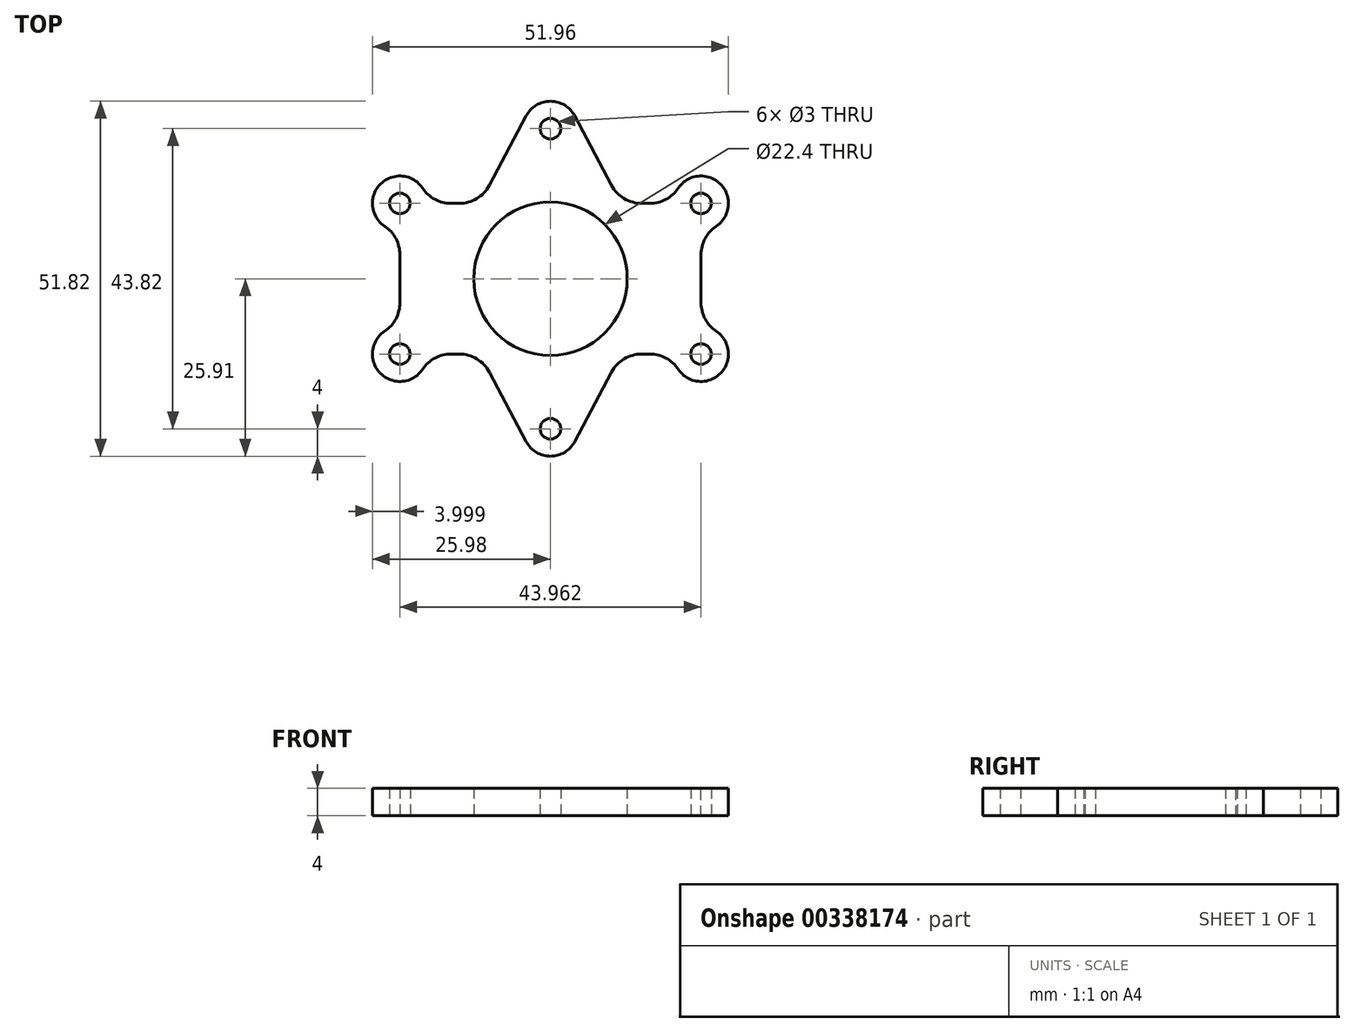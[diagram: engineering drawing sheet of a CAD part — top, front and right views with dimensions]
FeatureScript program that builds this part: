
annotation { "Feature Type Name" : "Feature", "Feature Type Description" : "" }
export const myFeature = defineFeature(function(context is Context, id is Id, definition is map)
    precondition{}
    {
        {
            var Q0;
            Q0=qCreatedBy(makeId("Top.planeOp"),FACE);
            var sketch = newSketch(context, id + "F0", { "sketchPlane" : qUnion([Q0])});
            skLineSegment(sketch, "E0.bottom", {"start": v(21.98, -11) * mm, "end": v(2.1, -11) * mm});
            skLineSegment(sketch, "E0.top", {"start": v(21.98, 11) * mm, "end": v(2.1, 11) * mm});
            skLineSegment(sketch, "E0.left", {"start": v(21.98, -11) * mm, "end": v(21.98, 11) * mm});
            skLineSegment(sketch, "E0.right", {"start": v(-21.98, -11) * mm, "end": v(-21.98, 11) * mm});
            skPoint(sketch, "E0.middle", {"position": v(0, 0) * mm});
            skCircle(sketch, "E1", {"center": v(0, 0) * mm, "radius": 11.2 * mm});
            skCircle(sketch, "E2", {"center": v(-21.98, 11) * mm, "radius": 1.5 * mm});
            skCircle(sketch, "E3", {"center": v(-21.98, -11) * mm, "radius": 1.5 * mm});
            skCircle(sketch, "E4", {"center": v(21.98, -11) * mm, "radius": 1.5 * mm});
            skCircle(sketch, "E5", {"center": v(21.98, 11) * mm, "radius": 1.5 * mm});
            skCircle(sketch, "E6", {"center": v(21.98, 11) * mm, "radius": 4 * mm});
            skCircle(sketch, "E7", {"center": v(21.98, -11) * mm, "radius": 4 * mm});
            skCircle(sketch, "E8", {"center": v(-21.98, -11) * mm, "radius": 4 * mm});
            skCircle(sketch, "E9", {"center": v(-21.98, 11) * mm, "radius": 4 * mm});
            skPoint(sketch, "E10", {"position": v(0, 21.91) * mm});
            skPoint(sketch, "E11", {"position": v(0, -21.91) * mm});
            skCircle(sketch, "E12", {"center": v(0, 21.91) * mm, "radius": 1.5 * mm});
            skCircle(sketch, "E13", {"center": v(0, -21.91) * mm, "radius": 1.5 * mm});
            skCircle(sketch, "E14", {"center": v(0, 21.91) * mm, "radius": 4 * mm});
            skCircle(sketch, "E15", {"center": v(0, -21.91) * mm, "radius": 4 * mm});
            skLineSegment(sketch, "E16", {"start": v(-21.98, 11) * mm, "end": v(-3.53, -23.78) * mm});
            skLineSegment(sketch, "E17", {"start": v(21.98, 11) * mm, "end": v(3.53, -23.78) * mm});
            skLineSegment(sketch, "E18", {"start": v(21.98, -11) * mm, "end": v(3.53, 23.78) * mm});
            skLineSegment(sketch, "E19", {"start": v(-21.98, -11) * mm, "end": v(-3.53, 23.78) * mm});
            skLineSegment(sketch, "E20.trimOffspring", {"start": v(-2.1, 11) * mm, "end": v(-21.98, 11) * mm});
            skLineSegment(sketch, "E21.trimOffspring", {"start": v(-2.1, -11) * mm, "end": v(-21.98, -11) * mm});
            skSolve(sketch);
        }
        {
            var Q0;
            {var subQ0=sQuery(id+"F0.wireOp",EDGE,"E21.trimOffspring");var subQ1=sQuery(id+"F0.wireOp",EDGE,"E8");var subQ2=makeQuery(id+"F0.imprint","INTERSECT",VERTEX,{"derivedFrom":[subQ1,subQ0]});Q0=makeQuery(id+"F0.imprint","IMPRINT",FACE,{"disambiguationData":[TD([[makeQuery(id+"F0.imprint","IMPRINT",EDGE,{"disambiguationData":[TD([[subQ2,-1.0]])],"derivedFrom":subQ1}),-1.0]])]});}
            var Q1;
            {var subQ5=sQuery(id+"F0.wireOp",EDGE,"E0.right");var subQ7=sQuery(id+"F0.wireOp",EDGE,"E8");var subQ8=makeQuery(id+"F0.imprint","INTERSECT",VERTEX,{"derivedFrom":[subQ5,subQ7]});Q1=makeQuery(id+"F0.imprint","IMPRINT",FACE,{"disambiguationData":[TD([[makeQuery(id+"F0.imprint","IMPRINT",EDGE,{"disambiguationData":[TD([[subQ8,-1.0]])],"derivedFrom":subQ5}),-1.0]])]});}
            var Q2;
            {var subQ0=sQuery(id+"F0.wireOp",EDGE,"E20.trimOffspring");var subQ1=sQuery(id+"F0.wireOp",EDGE,"E9");var subQ2=makeQuery(id+"F0.imprint","INTERSECT",VERTEX,{"derivedFrom":[subQ1,subQ0]});Q2=makeQuery(id+"F0.imprint","IMPRINT",FACE,{"disambiguationData":[TD([[makeQuery(id+"F0.imprint","IMPRINT",EDGE,{"disambiguationData":[TD([[subQ2,1.0]])],"derivedFrom":subQ1}),-1.0]])]});}
            var Q3;
            {var subQ0=sQuery(id+"F0.wireOp",EDGE,"E20.trimOffspring");var subQ1=sQuery(id+"F0.wireOp",EDGE,"E2");var subQ2=makeQuery(id+"F0.imprint","INTERSECT",VERTEX,{"derivedFrom":[subQ1,subQ0]});Q3=makeQuery(id+"F0.imprint","IMPRINT",FACE,{"disambiguationData":[TD([[makeQuery(id+"F0.imprint","IMPRINT",EDGE,{"disambiguationData":[TD([[subQ2,1.0]])],"derivedFrom":subQ1}),-1.0]])]});}
            var Q4;
            {var subQ0=sQuery(id+"F0.wireOp",EDGE,"E9");var subQ1=sQuery(id+"F0.wireOp",EDGE,"E0.right");var subQ2=makeQuery(id+"F0.imprint","INTERSECT",VERTEX,{"derivedFrom":[subQ1,subQ0]});Q4=makeQuery(id+"F0.imprint","IMPRINT",FACE,{"disambiguationData":[TD([[makeQuery(id+"F0.imprint","IMPRINT",EDGE,{"disambiguationData":[TD([[subQ2,-1.0]])],"derivedFrom":subQ1}),1.0]])]});}
            var Q5;
            {var subQ0=sQuery(id+"F0.wireOp",EDGE,"E9");var subQ1=sQuery(id+"F0.wireOp",EDGE,"E0.right");var subQ2=makeQuery(id+"F0.imprint","INTERSECT",VERTEX,{"derivedFrom":[subQ1,subQ0]});Q5=makeQuery(id+"F0.imprint","IMPRINT",FACE,{"disambiguationData":[TD([[makeQuery(id+"F0.imprint","IMPRINT",EDGE,{"disambiguationData":[TD([[subQ2,-1.0]])],"derivedFrom":subQ1}),-1.0]])]});}
            var Q6;
            {var subQ0=sQuery(id+"F0.wireOp",EDGE,"E8");var subQ1=sQuery(id+"F0.wireOp",EDGE,"E0.right");var subQ2=makeQuery(id+"F0.imprint","INTERSECT",VERTEX,{"derivedFrom":[subQ1,subQ0]});Q6=makeQuery(id+"F0.imprint","IMPRINT",FACE,{"disambiguationData":[TD([[makeQuery(id+"F0.imprint","IMPRINT",EDGE,{"disambiguationData":[TD([[subQ2,1.0]])],"derivedFrom":subQ1}),-1.0]])]});}
            var Q7;
            {var subQ0=sQuery(id+"F0.wireOp",EDGE,"E19");var subQ1=sQuery(id+"F0.wireOp",EDGE,"E3");var subQ2=makeQuery(id+"F0.imprint","INTERSECT",VERTEX,{"derivedFrom":[subQ1,subQ0]});Q7=makeQuery(id+"F0.imprint","IMPRINT",FACE,{"disambiguationData":[TD([[makeQuery(id+"F0.imprint","IMPRINT",EDGE,{"disambiguationData":[TD([[subQ2,1.0]])],"derivedFrom":subQ1}),-1.0]])]});}
            var Q8;
            {var subQ0=sQuery(id+"F0.wireOp",EDGE,"E8");var subQ1=sQuery(id+"F0.wireOp",EDGE,"E0.right");var subQ2=makeQuery(id+"F0.imprint","INTERSECT",VERTEX,{"derivedFrom":[subQ1,subQ0]});Q8=makeQuery(id+"F0.imprint","IMPRINT",FACE,{"disambiguationData":[TD([[makeQuery(id+"F0.imprint","IMPRINT",EDGE,{"disambiguationData":[TD([[subQ2,1.0]])],"derivedFrom":subQ1}),1.0]])]});}
            var Q9;
            {var subQ0=sQuery(id+"F0.wireOp",EDGE,"E7");var subQ1=sQuery(id+"F0.wireOp",EDGE,"E0.bottom");var subQ2=makeQuery(id+"F0.imprint","INTERSECT",VERTEX,{"derivedFrom":[subQ1,subQ0]});Q9=makeQuery(id+"F0.imprint","IMPRINT",FACE,{"disambiguationData":[TD([[makeQuery(id+"F0.imprint","IMPRINT",EDGE,{"disambiguationData":[TD([[subQ2,1.0]])],"derivedFrom":subQ1}),-1.0]])]});}
            var Q10;
            {var subQ0=sQuery(id+"F0.wireOp",EDGE,"E7");var subQ1=sQuery(id+"F0.wireOp",EDGE,"E0.left");var subQ2=makeQuery(id+"F0.imprint","INTERSECT",VERTEX,{"derivedFrom":[subQ1,subQ0]});Q10=makeQuery(id+"F0.imprint","IMPRINT",FACE,{"disambiguationData":[TD([[makeQuery(id+"F0.imprint","IMPRINT",EDGE,{"disambiguationData":[TD([[subQ2,1.0]])],"derivedFrom":subQ1}),1.0]])]});}
            var Q11;
            {var subQ0=sQuery(id+"F0.wireOp",EDGE,"E7");var subQ1=sQuery(id+"F0.wireOp",EDGE,"E0.bottom");var subQ2=makeQuery(id+"F0.imprint","INTERSECT",VERTEX,{"derivedFrom":[subQ1,subQ0]});Q11=makeQuery(id+"F0.imprint","IMPRINT",FACE,{"disambiguationData":[TD([[makeQuery(id+"F0.imprint","IMPRINT",EDGE,{"disambiguationData":[TD([[subQ2,1.0]])],"derivedFrom":subQ1}),1.0]])]});}
            var Q12;
            {var subQ0=sQuery(id+"F0.wireOp",EDGE,"E6");var subQ1=sQuery(id+"F0.wireOp",EDGE,"E0.top");var subQ2=makeQuery(id+"F0.imprint","INTERSECT",VERTEX,{"derivedFrom":[subQ1,subQ0]});Q12=makeQuery(id+"F0.imprint","IMPRINT",FACE,{"disambiguationData":[TD([[makeQuery(id+"F0.imprint","IMPRINT",EDGE,{"disambiguationData":[TD([[subQ2,1.0]])],"derivedFrom":subQ1}),1.0]])]});}
            var Q13;
            {var subQ0=sQuery(id+"F0.wireOp",EDGE,"E6");var subQ1=sQuery(id+"F0.wireOp",EDGE,"E0.left");var subQ2=makeQuery(id+"F0.imprint","INTERSECT",VERTEX,{"derivedFrom":[subQ1,subQ0]});Q13=makeQuery(id+"F0.imprint","IMPRINT",FACE,{"disambiguationData":[TD([[makeQuery(id+"F0.imprint","IMPRINT",EDGE,{"disambiguationData":[TD([[subQ2,-1.0]])],"derivedFrom":subQ1}),1.0]])]});}
            var Q14;
            {var subQ0=sQuery(id+"F0.wireOp",EDGE,"E6");var subQ1=sQuery(id+"F0.wireOp",EDGE,"E0.top");var subQ2=makeQuery(id+"F0.imprint","INTERSECT",VERTEX,{"derivedFrom":[subQ1,subQ0]});Q14=makeQuery(id+"F0.imprint","IMPRINT",FACE,{"disambiguationData":[TD([[makeQuery(id+"F0.imprint","IMPRINT",EDGE,{"disambiguationData":[TD([[subQ2,1.0]])],"derivedFrom":subQ1}),-1.0]])]});}
            var Q15;
            {var subQ5=sQuery(id+"F0.wireOp",EDGE,"E7");var subQ6=sQuery(id+"F0.wireOp",EDGE,"E0.left");var subQ7=makeQuery(id+"F0.imprint","INTERSECT",VERTEX,{"derivedFrom":[subQ6,subQ5]});Q15=makeQuery(id+"F0.imprint","IMPRINT",FACE,{"disambiguationData":[TD([[makeQuery(id+"F0.imprint","IMPRINT",EDGE,{"disambiguationData":[TD([[subQ7,-1.0]])],"derivedFrom":subQ6}),1.0]])]});}
            var Q16;
            {var subQ0=sQuery(id+"F0.wireOp",EDGE,"E6");var subQ1=sQuery(id+"F0.wireOp",EDGE,"E0.top");var subQ2=makeQuery(id+"F0.imprint","INTERSECT",VERTEX,{"derivedFrom":[subQ1,subQ0]});Q16=makeQuery(id+"F0.imprint","IMPRINT",FACE,{"disambiguationData":[TD([[makeQuery(id+"F0.imprint","IMPRINT",EDGE,{"disambiguationData":[TD([[subQ2,-1.0]])],"derivedFrom":subQ1}),1.0]])]});}
            var Q17;
            {var subQ0=sQuery(id+"F0.wireOp",EDGE,"E7");var subQ1=sQuery(id+"F0.wireOp",EDGE,"E0.bottom");var subQ2=makeQuery(id+"F0.imprint","INTERSECT",VERTEX,{"derivedFrom":[subQ1,subQ0]});Q17=makeQuery(id+"F0.imprint","IMPRINT",FACE,{"disambiguationData":[TD([[makeQuery(id+"F0.imprint","IMPRINT",EDGE,{"disambiguationData":[TD([[subQ2,-1.0]])],"derivedFrom":subQ1}),-1.0]])]});}
            var Q18;
            {var subQ1=sQuery(id+"F0.wireOp",EDGE,"E0.bottom");var subQ5=sQuery(id+"F0.wireOp",EDGE,"E1");var subQ6=makeQuery(id+"F0.imprint","INTERSECT",VERTEX,{"derivedFrom":[subQ1,subQ5]});Q18=makeQuery(id+"F0.imprint","IMPRINT",FACE,{"disambiguationData":[TD([[makeQuery(id+"F0.imprint","IMPRINT",EDGE,{"disambiguationData":[TD([[subQ6,1.0]])],"derivedFrom":subQ1}),-1.0]])]});}
            var Q19;
            {var subQ0=sQuery(id+"F0.wireOp",EDGE,"E20.trimOffspring");var subQ1=sQuery(id+"F0.wireOp",EDGE,"E1");var subQ2=makeQuery(id+"F0.imprint","INTERSECT",VERTEX,{"derivedFrom":[subQ1,subQ0]});Q19=makeQuery(id+"F0.imprint","IMPRINT",FACE,{"disambiguationData":[TD([[makeQuery(id+"F0.imprint","IMPRINT",EDGE,{"disambiguationData":[TD([[subQ2,-1.0]])],"derivedFrom":subQ1}),-1.0]])]});}
            var Q20;
            {var subQ7=sQuery(id+"F0.wireOp",EDGE,"E1");var subQ8=sQuery(id+"F0.wireOp",EDGE,"E0.bottom");var subQ9=makeQuery(id+"F0.imprint","INTERSECT",VERTEX,{"derivedFrom":[subQ8,subQ7]});Q20=makeQuery(id+"F0.imprint","IMPRINT",FACE,{"disambiguationData":[TD([[makeQuery(id+"F0.imprint","IMPRINT",EDGE,{"disambiguationData":[TD([[subQ9,1.0]])],"derivedFrom":subQ8}),1.0]])]});}
            var Q21;
            {var subQ3=sQuery(id+"F0.wireOp",EDGE,"E0.top");var subQ9=sQuery(id+"F0.wireOp",EDGE,"E1");var subQ10=makeQuery(id+"F0.imprint","INTERSECT",VERTEX,{"derivedFrom":[subQ3,subQ9]});Q21=makeQuery(id+"F0.imprint","IMPRINT",FACE,{"disambiguationData":[TD([[makeQuery(id+"F0.imprint","IMPRINT",EDGE,{"disambiguationData":[TD([[subQ10,1.0]])],"derivedFrom":subQ3}),-1.0]])]});}
            var Q22;
            Q22=makeQuery(id+"F0.imprint","IMPRINT",FACE,{"disambiguationData":[TD([[makeQuery(id+"F0.imprint","IMPRINT",EDGE,{"derivedFrom":sQuery(id+"F0.wireOp",EDGE,"E12")}),-1.0]])]});
            var Q23;
            Q23=makeQuery(id+"F0.imprint","IMPRINT",FACE,{"disambiguationData":[TD([[makeQuery(id+"F0.imprint","IMPRINT",EDGE,{"derivedFrom":sQuery(id+"F0.wireOp",EDGE,"E13")}),-1.0]])]});
            extrude(context, id + "F1", {"entities" : qUnion([Q0, Q1, Q2, Q3, Q4, Q5, Q6, Q7, Q8, Q9, Q10, Q11, Q12, Q13, Q14, Q15, Q16, Q17, Q18, Q19, Q20, Q21, Q22, Q23]), "depth" : 4 * mm, "offsetDistance" : 25 * mm});
        }
        {
            var Q0;
            Q0=makeQuery(id+"F1.opExtrude","SWEPT_EDGE",EDGE,{"disambiguationData":[OSD([sQuery(id+"F0.wireOp",EDGE,"E8"),sQuery(id+"F0.wireOp",EDGE,"E21.trimOffspring")])]});
            var Q1;
            Q1=makeQuery(id+"F1.opExtrude","SWEPT_EDGE",EDGE,{"disambiguationData":[OSD([sQuery(id+"F0.wireOp",EDGE,"E16"),sQuery(id+"F0.wireOp",EDGE,"E21.trimOffspring")])]});
            var Q2;
            Q2=makeQuery(id+"F1.opExtrude","SWEPT_EDGE",EDGE,{"disambiguationData":[OSD([sQuery(id+"F0.wireOp",EDGE,"E0.right"),sQuery(id+"F0.wireOp",EDGE,"E9")])]});
            var Q3;
            Q3=makeQuery(id+"F1.opExtrude","SWEPT_EDGE",EDGE,{"disambiguationData":[OSD([sQuery(id+"F0.wireOp",EDGE,"E0.right"),sQuery(id+"F0.wireOp",EDGE,"E8")])]});
            var Q4;
            Q4=makeQuery(id+"F1.opExtrude","SWEPT_EDGE",EDGE,{"disambiguationData":[OSD([sQuery(id+"F0.wireOp",EDGE,"E9"),sQuery(id+"F0.wireOp",EDGE,"E20.trimOffspring")])]});
            var Q5;
            Q5=makeQuery(id+"F1.opExtrude","SWEPT_EDGE",EDGE,{"disambiguationData":[OSD([sQuery(id+"F0.wireOp",EDGE,"E19"),sQuery(id+"F0.wireOp",EDGE,"E20.trimOffspring")])]});
            var Q6;
            Q6=makeQuery(id+"F1.opExtrude","SWEPT_EDGE",EDGE,{"disambiguationData":[OSD([sQuery(id+"F0.wireOp",EDGE,"E0.top"),sQuery(id+"F0.wireOp",EDGE,"E18")])]});
            var Q7;
            Q7=makeQuery(id+"F1.opExtrude","SWEPT_EDGE",EDGE,{"disambiguationData":[OSD([sQuery(id+"F0.wireOp",EDGE,"E0.top"),sQuery(id+"F0.wireOp",EDGE,"E6")])]});
            var Q8;
            Q8=makeQuery(id+"F1.opExtrude","SWEPT_EDGE",EDGE,{"disambiguationData":[OSD([sQuery(id+"F0.wireOp",EDGE,"E0.left"),sQuery(id+"F0.wireOp",EDGE,"E6")])]});
            var Q9;
            Q9=makeQuery(id+"F1.opExtrude","SWEPT_EDGE",EDGE,{"disambiguationData":[OSD([sQuery(id+"F0.wireOp",EDGE,"E0.left"),sQuery(id+"F0.wireOp",EDGE,"E7")])]});
            var Q10;
            Q10=makeQuery(id+"F1.opExtrude","SWEPT_EDGE",EDGE,{"disambiguationData":[OSD([sQuery(id+"F0.wireOp",EDGE,"E0.bottom"),sQuery(id+"F0.wireOp",EDGE,"E7")])]});
            var Q11;
            Q11=makeQuery(id+"F1.opExtrude","SWEPT_EDGE",EDGE,{"disambiguationData":[OSD([sQuery(id+"F0.wireOp",EDGE,"E0.bottom"),sQuery(id+"F0.wireOp",EDGE,"E17")])]});
            fillet(context, id + "F2", {"entities" : qUnion([Q0, Q1, Q2, Q3, Q4, Q5, Q6, Q7, Q8, Q9, Q10, Q11]), "radius" : 5 * mm, "tangentPropagation" : true, "allowEdgeOverflow" : false});
        }
    });
